SOLIDWORKS PART (.sldprt)
format: sldprt  version: not decoded by parser v0  size: 156,672 bytes
history: native  units: mm
features: sketch x5, extrude x3, cut_extrude x2, material x1 (+12 scaffold rows collapsed)
feature tree (23):
  scaffold x12  (default folders/planes/origin — collapsed)
  material  "ABS"
  sketch  "Sketch1"  dims[D1=42.0mm D2=21.3mm]
  extrude  "Boss-Extrude1"  Depth=3mm
  sketch  "Sketch2"  dims[D2=6.0mm D1=8.5mm D3=7.0mm D4=7.0mm]
  cut_extrude  "Cut-Extrude1"  Depth=3mm
  sketch  "Sketch4"  dims[D2=5.0mm D7=3.0mm D8=27.0mm D1=42.0mm D3=~5.500179mm D4=15.5mm D5=31.0mm D6=31.0mm]
  extrude  "Boss-Extrude2"  Depth=3mm
  sketch  "Sketch5"
  extrude  "Boss-Extrude3"  Depth=5mm
  sketch  "Sketch6"
  cut_extrude  "Cut-Extrude2"  Depth=20mm
decode coverage: 8 of 10 modeling features carry decoded parameters
note: ~ marks probable driven/reference dimensions
note: suppression state not decoded; provenance and decode notes live in map.json
